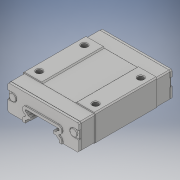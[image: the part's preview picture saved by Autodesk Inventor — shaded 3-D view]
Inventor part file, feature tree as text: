
AUTODESK INVENTOR PART (.ipt)
format: ipt  version: 2019 (Build 230136000, 136)  size: 508,928 bytes
history: native  units: mm
features: sketch x21, extrude x16, other x7, revolve x4, hole x1, pattern_linear x1
ambient origin geometry x8: Origin, YZ Plane, XZ Plane, XY Plane, X Axis, Y Axis, Z Axis, Center Point
bodies: Solid1 (feature_tree)
feature tree (50):
  extrude  "Extrusion1"  Depth=7.5mm TaperAngle=0.0deg
  extrude  "Extrusion2"  Depth=1.5mm TaperAngle=0.0deg
  extrude  "Extrusion3"  Depth=1.5mm TaperAngle=0.0deg
  extrude  "Extrusion4"  Depth=0.6mm TaperAngle=0.0deg
  extrude  "Extrusion5"  Depth=0.6mm TaperAngle=0.0deg
  extrude  "Extrusion6"  TaperAngle=360.0deg  [1 undecoded]
  extrude  "Extrusion7"  TaperAngle=360.0deg  [1 undecoded]
  extrude  "Extrusion8"  Depth=27.4mm TaperAngle=0.0deg
  extrude  "Extrusion9"  Depth=0.05mm TaperAngle=0.0deg
  extrude  "Extrusion10"  Depth=0.05mm TaperAngle=0.0deg
  extrude  "Extrusion11"  Depth=7.0mm
  revolve  "Revolution1"  [1 undecoded]
  revolve  "Revolution2"  [1 undecoded]
  revolve  "Revolution3"  [1 undecoded]
  revolve  "Revolution4"  [1 undecoded]
  extrude  "Extrusion12"  [1 undecoded]
  extrude  "Extrusion13"  [1 undecoded]
  extrude  "Extrusion14"  [1 undecoded]
  extrude  "Extrusion15"  [1 undecoded]
  extrude  "Extrusion16"  [1 undecoded]
  hole  "Hole1"  [1 undecoded]
  pattern_linear  "Rectangular Pattern1"  [2 undecoded]
  other  "to_rail_XY"
  other  "to_rail_YZ"
  other  "to_rail_ZX"
  other  "to_rail_X"
  other  "to_rail_Y"
  other  "to_rail_Z"
  other  "to_rail_Center"
  sketch  "Sketch_2"  dims[d0=27.4mm d1=0.0mm d2=7.5mm d3=0.0mm]
  sketch  "Sketch_3"  dims[d4=7.5mm d5=0.0mm d6=1.5mm d7=0.0mm]
  sketch  "Sketch_4"  dims[d8=0.5mm d9=0.0mm d10=1.5mm d11=0.0mm]
  sketch  "Sketch_8"  dims[d20=0.6mm d21=0.0mm d22=360.0deg]
  sketch  "Sketch_15"  dims[d36=2.459mm d37=4.0mm d38=3.0mm d39=2.0mm d40=90.0deg d41=7.0mm d42=120.0deg d43=20.0mm d45=25.0mm d46=20.0mm d48=20.0mm]
  sketch  "Sketch_7"  dims[d16=0.6mm d17=0.0mm d18=0.6mm d19=0.0mm]
  sketch  "Sketch_13"  dims[d32=13.7mm d33=0.0mm d34=0.05mm d35=0.0mm]
  sketch  "Sketch_25"
  sketch  "Sketch_5"  dims[d12=0.5mm d13=0.0mm d14=0.6mm d15=0.0mm]
  sketch  "Sketch_9"  dims[d23=360.0deg d24=360.0deg]
  sketch  "Sketch_26"
  sketch  "Sketch_18"
  sketch  "Sketch_19"
  sketch  "Sketch_20"
  sketch  "Sketch_21"
  sketch  "Sketch_17"
  sketch  "Sketch_11"  dims[d28=13.7mm d29=0.0mm d30=0.05mm d31=0.0mm]
  sketch  "Sketch_22"
  sketch  "Sketch_10"  dims[d25=360.0deg d26=27.4mm d27=0.0mm]
  sketch  "Sketch_23"
  sketch  "Sketch21"
note: 14 required parameter values undecoded (feature->parameter linkage not recoverable at this tier; creation-order binding heuristic only, values carry confidence <= 0.55)
